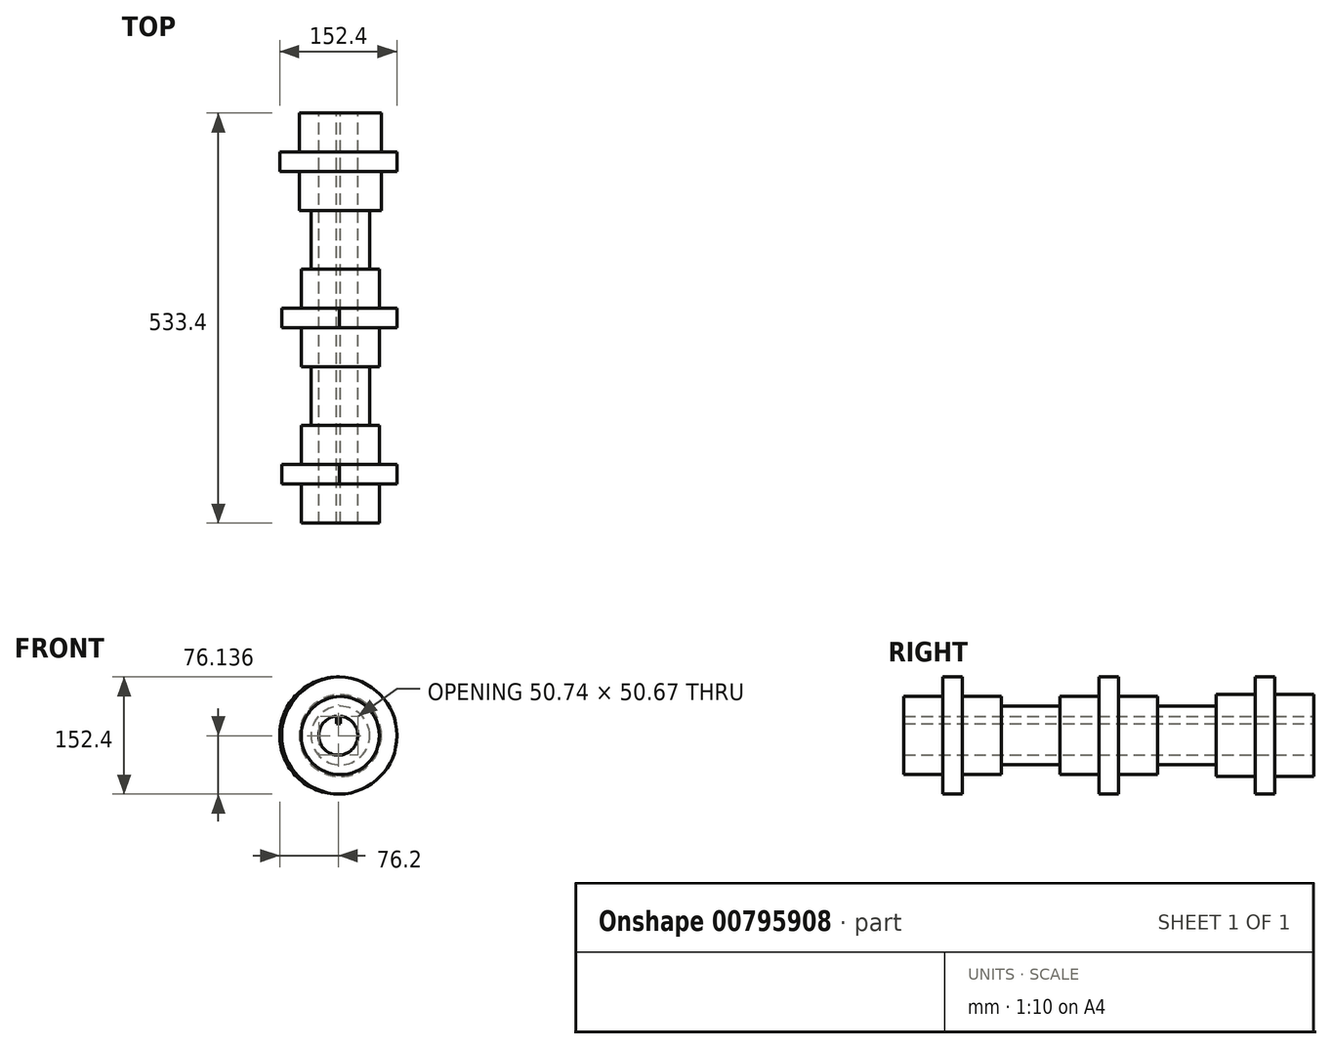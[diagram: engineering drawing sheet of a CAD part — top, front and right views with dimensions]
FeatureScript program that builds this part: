
annotation { "Feature Type Name" : "Feature", "Feature Type Description" : "" }
export const myFeature = defineFeature(function(context is Context, id is Id, definition is map)
    precondition{}
    {
        {
            var Q0;
            Q0=qCreatedBy(makeId("Front.planeOp"),FACE);
            var sketch = newSketch(context, id + "F0", { "sketchPlane" : qUnion([Q0])});
            skArc(sketch, "E0", {"start": v(-2.54, 25.27) * mm, "mid": v(0, -25.4) * mm, "end": v(2.54, 25.27) * mm});
            skCircle(sketch, "E1", {"center": v(0, 0) * mm, "radius": 76.2 * mm});
            skLineSegment(sketch, "E2.bottom", {"start": v(2.58, 15.24) * mm, "end": v(-2.5, 15.24) * mm});
            skLineSegment(sketch, "E2.left", {"start": v(2.54, 25.27) * mm, "end": v(2.58, 15.24) * mm});
            skLineSegment(sketch, "E2.right", {"start": v(-2.54, 25.27) * mm, "end": v(-2.5, 15.24) * mm});
            skPoint(sketch, "E2.middle", {"position": v(0, 25.4) * mm});
            skPoint(sketch, "E3.orphan", {"position": v(2.5, 35.56) * mm});
            skPoint(sketch, "E4.orphan", {"position": v(-2.58, 35.56) * mm});
            skSolve(sketch);
        }
        {
            var Q0;
            Q0 = qSketchRegion(id + "F0", true);
            extrude(context, id + "F1", {"entities" : qUnion([Q0]), "depth" : 533.4 * mm, "offsetDistance" : 25.4 * mm});
        }
        {
            var Q0;
            Q0=qCreatedBy(makeId("Top.planeOp"),FACE);
            var sketch = newSketch(context, id + "F2", { "sketchPlane" : qUnion([Q0])});
            skLineSegment(sketch, "E5", {"start": v(-50.8, 0) * mm, "end": v(-50.8, -50.8) * mm});
            skLineSegment(sketch, "E6", {"start": v(-50.8, -50.8) * mm, "end": v(-76.2, -50.8) * mm});
            skLineSegment(sketch, "E7", {"start": v(-76.2, -50.8) * mm, "end": v(-76.2, -76.2) * mm});
            skLineSegment(sketch, "E8", {"start": v(-76.2, -76.2) * mm, "end": v(-50.8, -76.2) * mm});
            skLineSegment(sketch, "E9", {"start": v(-50.8, -76.2) * mm, "end": v(-50.8, -127) * mm});
            skLineSegment(sketch, "E10", {"start": v(-89.3, -127) * mm, "end": v(-89.3, 0) * mm});
            skLineSegment(sketch, "E11", {"start": v(-89.3, 0) * mm, "end": v(-50.8, 0) * mm});
            skLineSegment(sketch, "E12", {"start": v(-48.22, -203.2) * mm, "end": v(-48.22, -254) * mm});
            skLineSegment(sketch, "E13", {"start": v(-48.22, -254) * mm, "end": v(-73.62, -254) * mm});
            skLineSegment(sketch, "E14", {"start": v(-73.62, -254) * mm, "end": v(-73.62, -279.4) * mm});
            skLineSegment(sketch, "E15", {"start": v(-73.62, -279.4) * mm, "end": v(-48.22, -279.4) * mm});
            skLineSegment(sketch, "E16", {"start": v(-48.22, -279.4) * mm, "end": v(-48.22, -330.2) * mm});
            skLineSegment(sketch, "E17", {"start": v(-89.3, -330.2) * mm, "end": v(-89.3, -203.2) * mm});
            skLineSegment(sketch, "E18", {"start": v(-48.22, -406.4) * mm, "end": v(-48.22, -457.2) * mm});
            skLineSegment(sketch, "E19", {"start": v(-48.22, -457.2) * mm, "end": v(-73.62, -457.2) * mm});
            skLineSegment(sketch, "E20", {"start": v(-73.62, -457.2) * mm, "end": v(-73.62, -482.6) * mm});
            skLineSegment(sketch, "E21", {"start": v(-73.62, -482.6) * mm, "end": v(-48.22, -482.6) * mm});
            skLineSegment(sketch, "E22", {"start": v(-48.22, -482.6) * mm, "end": v(-48.22, -533.4) * mm});
            skLineSegment(sketch, "E23", {"start": v(-48.22, -533.4) * mm, "end": v(-86.32, -533.4) * mm});
            skLineSegment(sketch, "E24", {"start": v(-86.32, -533.4) * mm, "end": v(-86.32, -406.4) * mm});
            skLineSegment(sketch, "E25.right", {"start": v(2.58, -127) * mm, "end": v(2.58, -203.2) * mm});
            skLineSegment(sketch, "E26", {"start": v(-50.8, -127) * mm, "end": v(-35.52, -127) * mm});
            skLineSegment(sketch, "E27", {"start": v(-35.52, -203.2) * mm, "end": v(-48.22, -203.2) * mm});
            skLineSegment(sketch, "E28", {"start": v(-89.3, -127) * mm, "end": v(-89.3, -203.2) * mm});
            skLineSegment(sketch, "E29", {"start": v(-89.3, -330.2) * mm, "end": v(-86.32, -406.4) * mm});
            skLineSegment(sketch, "E30", {"start": v(-48.22, -330.2) * mm, "end": v(-35.52, -330.2) * mm});
            skLineSegment(sketch, "E31", {"start": v(-35.52, -406.4) * mm, "end": v(-48.22, -406.4) * mm});
            skLineSegment(sketch, "E32", {"start": v(-35.52, -127) * mm, "end": v(-35.52, -203.2) * mm});
            skLineSegment(sketch, "E33", {"start": v(-35.52, -330.2) * mm, "end": v(-35.52, -406.4) * mm});
            skSolve(sketch);
        }
        {
            var Q0;
            Q0 = qSketchRegion(id + "F2", true);
            var Q1;
            Q1=sQuery(id+"F2.wireOp",EDGE,"E25.right");
            revolve(context, id + "F3", {"operationType" : NewBodyOperationType.REMOVE, "surfaceOperationType" : NewSurfaceOperationType.NEW, "entities" : qUnion([Q0]), "axis" : qUnion([Q1]), "revolveType" : RevolveType.FULL, "oppositeDirection" : true});
        }
    });
